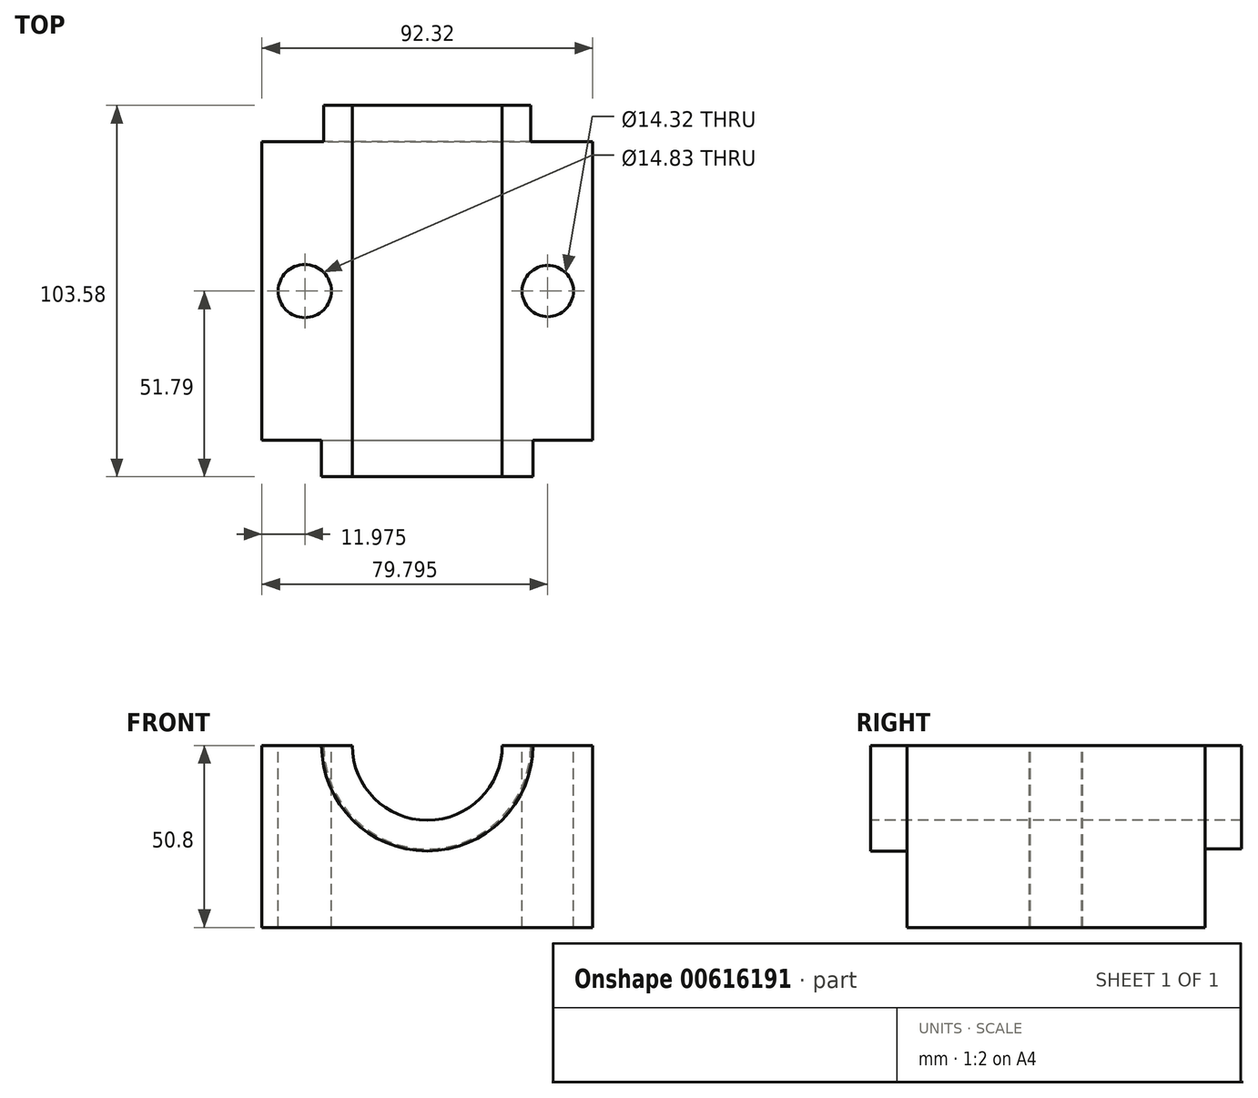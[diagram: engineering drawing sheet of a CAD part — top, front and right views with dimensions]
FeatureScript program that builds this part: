
annotation { "Feature Type Name" : "Feature", "Feature Type Description" : "" }
export const myFeature = defineFeature(function(context is Context, id is Id, definition is map)
    precondition{}
    {
        {
            var Q0;
            Q0=qCreatedBy(makeId("Top.planeOp"),FACE);
            var sketch = newSketch(context, id + "F0", { "sketchPlane" : qUnion([Q0])});
            skLineSegment(sketch, "E0.bottom", {"start": v(-46.16, 41.63) * mm, "end": v(46.16, 41.63) * mm});
            skLineSegment(sketch, "E0.top", {"start": v(-46.16, -41.63) * mm, "end": v(46.16, -41.63) * mm});
            skLineSegment(sketch, "E0.left", {"start": v(-46.16, 41.63) * mm, "end": v(-46.16, -41.63) * mm});
            skLineSegment(sketch, "E0.right", {"start": v(46.16, 41.63) * mm, "end": v(46.16, -41.63) * mm});
            skPoint(sketch, "E0.middle", {"position": v(0, 0) * mm});
            skSolve(sketch);
        }
        {
            var Q0;
            Q0=makeQuery(id+"F0.imprint","IMPRINT",FACE,{"disambiguationData":[TD([[makeQuery(id+"F0.imprint","IMPRINT",EDGE,{"derivedFrom":sQuery(id+"F0.wireOp",EDGE,"E0.bottom")}),-1.0]])]});
            extrude(context, id + "F1", {"entities" : qUnion([Q0]), "depth" : 50.8 * mm, "offsetDistance" : 25.4 * mm});
        }
        {
            var Q0;
            Q0=makeQuery(id+"F1.opExtrude","SWEPT_FACE",FACE,{"disambiguationData":[OSD([sQuery(id+"F0.wireOp",EDGE,"E0.top")])]});
            var sketch = newSketch(context, id + "F2", { "sketchPlane" : qUnion([Q0])});
            skArc(sketch, "E1", {"start": v(-20.92, 50.8) * mm, "mid": v(0, 29.88) * mm, "end": v(20.92, 50.8) * mm});
            skLineSegment(sketch, "E2", {"start": v(-20.92, 50.8) * mm, "end": v(20.92, 50.8) * mm});
            skSolve(sketch);
        }
        {
            var Q0;
            {var subQ3=sQuery(id+"F2.wireOp",EDGE,"E1");Q0=makeQuery(id+"F2.imprint","IMPRINT",FACE,{"disambiguationData":[TD([[makeQuery(id+"F2.imprint","IMPRINT",EDGE,{"derivedFrom":subQ3}),-1.0]])]});}
            var sketch = newSketch(context, id + "F3", { "sketchPlane" : qUnion([Q0])});
            skArc(sketch, "E3", {"start": v(-29.5, 51.15) * mm, "mid": v(0, 21.34) * mm, "end": v(29.5, 51.15) * mm});
            skLineSegment(sketch, "E4", {"start": v(-29.5, 51.15) * mm, "end": v(29.5, 51.15) * mm});
            skSolve(sketch);
        }
        {
            var Q0;
            Q0=makeQuery(id+"F2.imprint","IMPRINT",FACE,{"disambiguationData":[TD([[makeQuery(id+"F2.imprint","IMPRINT",EDGE,{"derivedFrom":sQuery(id+"F2.wireOp",EDGE,"E1")}),1.0]])]});
            extrude(context, id + "F4", {"entities" : qUnion([Q0]), "operationType" : NewBodyOperationType.REMOVE, "oppositeDirection" : true, "depth" : 127 * mm, "offsetDistance" : 25.4 * mm});
        }
        {
            var Q0;
            {var subQ4=sQuery(id+"F2.wireOp",EDGE,"E1");var subQ9=makeQuery(id+"F2.imprint","IMPRINT",EDGE,{"derivedFrom":subQ4});Q0=makeQuery(id+"F3.imprint","IMPRINT",FACE,{"disambiguationData":[TD([[makeQuery(id+"F3.imprint","IMPRINT",EDGE,{"derivedFrom":subQ9}),-1.0]])]});}
            extrude(context, id + "F5", {"entities" : qUnion([Q0]), "operationType" : NewBodyOperationType.ADD, "depth" : 10.16 * mm, "offsetDistance" : 25.4 * mm});
        }
        {
            var Q0;
            Q0=makeQuery(id+"F1.opExtrude","SWEPT_FACE",FACE,{"disambiguationData":[OSD([sQuery(id+"F0.wireOp",EDGE,"E0.bottom")])]});
            var sketch = newSketch(context, id + "F6", { "sketchPlane" : qUnion([Q0])});
            skArc(sketch, "E5", {"start": v(-28.88, 50.8) * mm, "mid": v(0, 21.92) * mm, "end": v(28.88, 50.8) * mm});
            skLineSegment(sketch, "E6", {"start": v(-28.88, 50.8) * mm, "end": v(-20.92, 50.8) * mm});
            skLineSegment(sketch, "E7", {"start": v(28.88, 50.8) * mm, "end": v(20.92, 50.8) * mm});
            skLineSegment(sketch, "E8.trimOffspring", {"start": v(20.92, 50.8) * mm, "end": v(28.88, 50.8) * mm});
            skSolve(sketch);
        }
        {
            var Q0;
            Q0=makeQuery(id+"F6.imprint","IMPRINT",FACE,{"disambiguationData":[TD([[makeQuery(id+"F6.imprint","IMPRINT",EDGE,{"derivedFrom":sQuery(id+"F6.wireOp",EDGE,"E5")}),1.0]])]});
            extrude(context, id + "F7", {"entities" : qUnion([Q0]), "operationType" : NewBodyOperationType.ADD, "depth" : 10.16 * mm, "offsetDistance" : 25.4 * mm});
        }
        {
            var Q0;
            {var subQ0=sQuery(id+"F0.wireOp",EDGE,"E0.top");var subQ1=makeQuery(id+"F1.opExtrude","CAP_EDGE",EDGE,{"disambiguationData":[OSD([subQ0])],"isStart":false});var subQ2=sQuery(id+"F0.wireOp",EDGE,"E0.right");var subQ3=sQuery(id+"F2.wireOp",EDGE,"E1");var subQ4=makeQuery(id+"F2.imprint","IMPRINT",EDGE,{"disambiguationData":[TD([[makeQuery(id+"F2.imprint","INTERSECT",VERTEX,{"derivedFrom":[makeQuery(id+"F1.opExtrude","SWEPT_EDGE",EDGE,{"disambiguationData":[OSD([subQ0,subQ2])]}),subQ1]}),1.0]])],"derivedFrom":subQ1});var subQ5=sQuery(id+"F0.wireOp",EDGE,"E0.bottom");Q0=makeQuery(id+"F7.boolean.opBoolean","MERGE",FACE,{"derivedFrom":[makeQuery(id+"F5.boolean.opBoolean","MERGE",FACE,{"derivedFrom":[makeQuery(id+"F4.boolean.opBoolean","SPLIT",FACE,{"disambiguationData":[TD([makeQuery(id+"F1.opExtrude","SWEPT_FACE",FACE,{"disambiguationData":[OSD([subQ2])]})])],"derivedFrom":makeQuery(id+"F1.opExtrude","CAP_FACE",FACE,{"disambiguationData":[OSD([subQ5,subQ0,sQuery(id+"F0.wireOp",EDGE,"E0.left"),subQ2])],"isStart":false})}),makeQuery(id+"F5.opExtrude","SWEPT_FACE",FACE,{"disambiguationData":[OSD([subQ0]),TDD([makeQuery(id+"F3.imprint","IMPRINT",EDGE,{"disambiguationData":[TD([[makeQuery(id+"F3.imprint","INTERSECT",VERTEX,{"derivedFrom":[makeQuery(id+"F2.imprint","IMPRINT",EDGE,{"derivedFrom":subQ3}),subQ4]}),-1.0]])],"derivedFrom":subQ4})])]})]}),makeQuery(id+"F7.opExtrude","SWEPT_FACE",FACE,{"disambiguationData":[OSD([sQuery(id+"F6.wireOp",EDGE,"E6")])]})]});}
            var sketch = newSketch(context, id + "F8", { "sketchPlane" : qUnion([Q0])});
            skCircle(sketch, "E9", {"center": v(33.64, 0) * mm, "radius": 7.16 * mm});
            skCircle(sketch, "E10", {"center": v(-34.19, 0) * mm, "radius": 7.41 * mm});
            skSolve(sketch);
        }
        {
            var Q0;
            Q0 = qSketchRegion(id + "F8", true);
            extrude(context, id + "F9", {"entities" : qUnion([Q0]), "operationType" : NewBodyOperationType.REMOVE, "oppositeDirection" : true, "depth" : 152.4 * mm, "offsetDistance" : 25.4 * mm});
        }
    });
